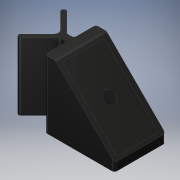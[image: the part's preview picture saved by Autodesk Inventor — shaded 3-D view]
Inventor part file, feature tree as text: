
AUTODESK INVENTOR PART (.ipt)
format: ipt  version: 2019 (Build 230136000, 136)  size: 296,960 bytes
history: native  units: mm
features: sketch x8, extrude x6, projected_geometry x4, fillet x3, hole x2, shell x1, chamfer x1
ambient origin geometry x8: Origin, YZ Plane, XZ Plane, XY Plane, X Axis, Y Axis, Z Axis, Center Point
bodies: Solid1 (feature_tree)
feature tree (25):
  extrude  "Extrusion1"  Depth=110.0mm
  extrude  "Extrusion2"  TaperAngle=45.0deg  [1 undecoded]
  shell  "Shell1"  Thickness=180.0mm
  extrude  "Extrusion3"  Depth=6.0mm
  hole  "Hole1"  [1 undecoded]
  extrude  "Extrusion4"  Depth=10.0mm
  fillet  "Fillet1"  Radius=2.5mm
  fillet  "Fillet2"  Radius=60.0mm
  chamfer  "Chamfer1"  Distance=15.0mm
  fillet  "Fillet3"  Radius=47.5mm
  hole  "Hole2"  [1 undecoded]
  extrude  "Extrusion5"  Depth=10.0mm
  extrude  "Extrusion6"  Depth=5.0mm
  sketch  "Sketch1"  dims[d0=150.0mm d1=110.0mm]
  sketch  "Sketch2"  dims[d2=150.0mm d3=0.0mm d4=45.0deg d6=180.0mm]
  projected_geometry  "Projected Loop1"
  sketch  "Sketch3"  dims[d7=150.0mm d8=0.0mm d9=6.0mm]
  sketch  "Sketch4"  dims[d10=166.0mm d11=90.0mm]
  sketch  "Sketch5"  dims[d12=7.0mm d13=10.0mm d14=2.5mm d15=0.0mm]
  sketch  "Sketch7"  dims[d16=27.0mm d17=6.0mm d18=4.0mm d19=2.0mm d20=90.0deg d21=12.0mm d22=20.594885mm d25=60.0mm]
  projected_geometry  "Projected Loop2"
  sketch  "Sketch8"  dims[d26=10.0mm]
  projected_geometry  "Projected Loop3"
  sketch  "Sketch10"  dims[d27=15.0mm d28=15.0mm d29=47.5mm d30=150.0mm d31=0.0mm d32=10.0mm d33=5.0mm d34=10.0mm d35=2.0mm d36=45.0deg d37=5.0mm d38=5.3mm d39=6.0mm d40=4.0mm d41=2.0mm d42=90.0deg d43=8.9mm d44=0.0mm d45=8.0mm d46=20.0mm d47=8.0mm d48=20.0mm d49=30.0mm d50=30.0mm d51=150.0mm d52=0.0mm d53=5.0mm d54=0.0mm]
  projected_geometry  "Projected Loop5"
note: 3 required parameter values undecoded (feature->parameter linkage not recoverable at this tier; creation-order binding heuristic only, values carry confidence <= 0.55)
